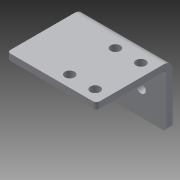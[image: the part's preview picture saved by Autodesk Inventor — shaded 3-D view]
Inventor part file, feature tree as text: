
AUTODESK INVENTOR PART (.ipt)
format: ipt  version: 2014 (Build 180170000, 170)  size: 188,416 bytes
history: native  units: in
note: dims shown in document units (in); Inventor stores cm internally (conversion verified against a paired STEP export)
features: sheet_metal_op x4, other x4, sketch x3, fillet x1, extrude x1
ambient origin geometry x8: Origin, YZ Plane, XZ Plane, XY Plane, X Axis, Y Axis, Z Axis, Center Point
bodies: Solid1 (feature_tree)
feature tree (13):
  sheet_metal_op  "Face1"
  sheet_metal_op  "Flange1"
  fillet  "Fillet1"  Radius=1.75in
  extrude  "Extrusion1"  Depth=0.19in
  sketch  "Sketch1"  dims[d1=1.0in d2=0.19in]
  other  "Plate1"
  sketch  "Sketch2"  dims[d4=0.7874in d6=1.0in d7=0.3937in d9=1.0in]
  other  "Plate2"
  sheet_metal_op  "Bend1"
  sheet_metal_op  "Corner1"
  sketch  "Sketch3"  dims[d11=0.125in d12=0.125in d13=0.0625in d14=0.25in d15=0.125in d16=1.5in d17=90.0deg d18=0.05in d19=0.5in d20=0.125in d21=0.125in d22=0.0625in d23=1.35in d24=0.75in d27=0.19in d28=0.125in d29=0.2265in d30=1.0in d31=0.0in d34=0.25in d35=0.875in d3=0.0in d5=0.1649in d8=0.025in]
  other  "Definition1"
  other  "Cut1"
